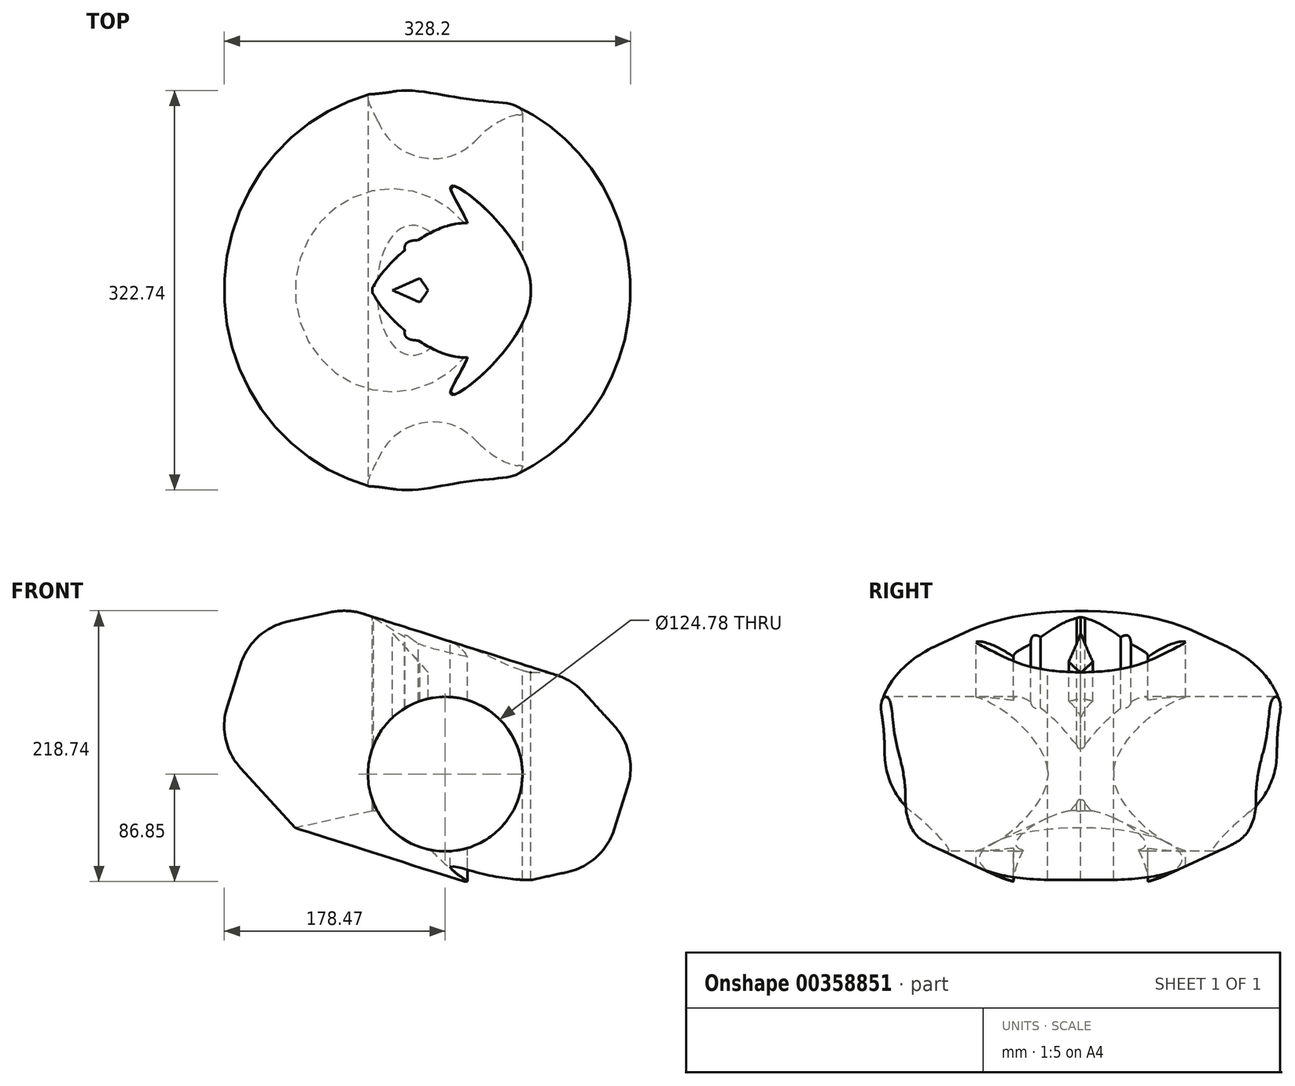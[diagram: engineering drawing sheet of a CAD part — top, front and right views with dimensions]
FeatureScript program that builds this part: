
annotation { "Feature Type Name" : "Feature", "Feature Type Description" : "" }
export const myFeature = defineFeature(function(context is Context, id is Id, definition is map)
    precondition{}
    {
        {
            var Q0;
            Q0=qCreatedBy(makeId("Front.planeOp"),FACE);
            var sketch = newSketch(context, id + "F0", { "sketchPlane" : qUnion([Q0])});
            skCircle(sketch, "E0.cCircle", {"center": v(-92.5, 46.77) * mm, "radius": 81.98 * mm, "construction": true});
            skLineSegment(sketch, "E0.0", {"start": v(-0.05, 67.07) * mm, "end": v(-28.7, -23.15) * mm});
            skLineSegment(sketch, "E0.1", {"start": v(-28.7, -23.15) * mm, "end": v(-121.16, -43.45) * mm});
            skLineSegment(sketch, "E0.2", {"start": v(-121.16, -43.45) * mm, "end": v(-184.97, 26.47) * mm});
            skLineSegment(sketch, "E0.3", {"start": v(-184.97, 26.47) * mm, "end": v(-156.32, 116.7) * mm});
            skLineSegment(sketch, "E0.4", {"start": v(-156.32, 116.7) * mm, "end": v(-63.86, 137) * mm});
            skLineSegment(sketch, "E0.5", {"start": v(-63.86, 137) * mm, "end": v(-0.05, 67.07) * mm});
            skPoint(sketch, "E0.0.midPoint", {"position": v(-14.37, 21.96) * mm});
            skCircle(sketch, "E1", {"center": v(17.2, 11.65) * mm, "radius": 26.54 * mm});
            skSolve(sketch);
        }
        {
            var Q0;
            Q0=makeQuery(id+"F0.imprint","IMPRINT",FACE,{"disambiguationData":[TD([[makeQuery(id+"F0.imprint","IMPRINT",EDGE,{"derivedFrom":sQuery(id+"F0.wireOp",EDGE,"E0.0")}),-1.0]])]});
            var Q1;
            Q1=sQuery(id+"F0.wireOp",EDGE,"E0.0");
            revolve(context, id + "F1", {"entities" : qUnion([Q0]), "axis" : qUnion([Q1]), "revolveType" : RevolveType.FULL});
        }
        {
            var Q0;
            Q0=makeQuery(id+"F1.opRevolve","SWEPT_EDGE",EDGE,{"disambiguationData":[OSD([sQuery(id+"F0.wireOp",EDGE,"E0.3"),sQuery(id+"F0.wireOp",EDGE,"E0.4")])]});
            var Q1;
            Q1=makeQuery(id+"F1.opRevolve","SWEPT_FACE",FACE,{"disambiguationData":[OSD([sQuery(id+"F0.wireOp",EDGE,"E0.3")])]});
            var Q2;
            Q2=makeQuery(id+"F1.opRevolve","SWEPT_EDGE",EDGE,{"disambiguationData":[OSD([sQuery(id+"F0.wireOp",EDGE,"E0.4"),sQuery(id+"F0.wireOp",EDGE,"E0.5")])]});
            fillet(context, id + "F2", {"entities" : qUnion([Q0, Q1, Q2]), "radius" : 50.8 * mm, "tangentPropagation" : true, "allowEdgeOverflow" : false});
        }
        {
            var Q0;
            Q0=qCreatedBy(makeId("Front.planeOp"),FACE);
            var sketch = newSketch(context, id + "F3", { "sketchPlane" : qUnion([Q0])});
            skCircle(sketch, "E2", {"center": v(0, 0) * mm, "radius": 62.39 * mm});
            skSolve(sketch);
        }
        {
            var Q0;
            Q0 = qSketchRegion(id + "F3", true);
            extrude(context, id + "F4", {"entities" : qUnion([Q0]), "operationType" : NewBodyOperationType.REMOVE, "endBound" : BoundingType.SYMMETRIC, "oppositeDirection" : true, "depth" : 1524 * mm});
        }
        {
            var Q0;
            Q0=qCreatedBy(makeId("Top.planeOp"),FACE);
            var sketch = newSketch(context, id + "F5", { "sketchPlane" : qUnion([Q0])});
            skFitSpline(sketch, "E3", {"points": [v(-32.27, -36.67) * mm, v(-8.3, 12.22) * mm, v(-57.2, -3.6) * mm, v(7.5, 53.44) * mm, v(67.9, -11.26) * mm, v(4.15, -83.64) * mm, v(18.53, -42.9) * mm, v(-32.27, -36.67) * mm]});
            skSolve(sketch);
        }
        {
            var Q0;
            Q0 = qSketchRegion(id + "F5", true);
            extrude(context, id + "F6", {"entities" : qUnion([Q0]), "operationType" : NewBodyOperationType.REMOVE, "endBound" : BoundingType.SYMMETRIC, "oppositeDirection" : true, "depth" : 1524 * mm, "hasSecondDirection" : true, "secondDirectionOppositeDirection" : false, "secondDirectionDepth" : 1016 * mm});
        }
        {
            var Q0;
            Q0=makeQuery(id+"F1.opRevolve","SWEPT_BODY",BODY,{"disambiguationData":[OSD([sQuery(id+"F0.wireOp",EDGE,"E0.0"),sQuery(id+"F0.wireOp",EDGE,"E0.1"),sQuery(id+"F0.wireOp",EDGE,"E0.2"),sQuery(id+"F0.wireOp",EDGE,"E0.3"),sQuery(id+"F0.wireOp",EDGE,"E0.4"),sQuery(id+"F0.wireOp",EDGE,"E0.5")])]});
            var Q1;
            Q1=qCreatedBy(makeId("Front.planeOp"),FACE);
            mirror(context, id + "F7", {"operationType" : NewBodyOperationType.INTERSECT, "entities" : qUnion([Q0]), "mirrorPlane" : qUnion([Q1])});
        }
    });
